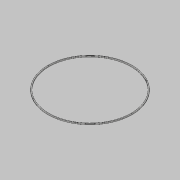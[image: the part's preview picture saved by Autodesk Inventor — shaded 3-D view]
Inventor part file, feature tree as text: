
AUTODESK INVENTOR PART (.ipt)
format: ipt  version: 2017 (Build 210142000, 142)  size: 189,440 bytes
history: native  units: in
note: dims shown in document units (in); Inventor stores cm internally (conversion verified against a paired STEP export)
features: other x1, sketch x1, sweep x1, extrude x1
ambient origin geometry x8: Origin, YZ Plane, XZ Plane, XY Plane, X Axis, Y Axis, Z Axis, Center Point
bodies: Solid1 (feature_tree)
feature tree (4):
  other  "FeedHoop37"
  sketch  "Sketch1"  dims[d1=60.0deg d2=60.0deg d23=0.0in d24=0.0in d25=0.0in d26=0.0in d28=0.315in d29=0.374in d30=2.3622in d32=360.0deg d34=0.748in d35=0.748in d36=0.0098in d37=0.063in d38=0.0098in]
  sweep  "Sweep1"
  extrude  "Extrusion1"  TaperAngle=0.0deg  [1 undecoded]
note: 1 required parameter value undecoded (feature->parameter linkage not recoverable at this tier; creation-order binding heuristic only, values carry confidence <= 0.55)
